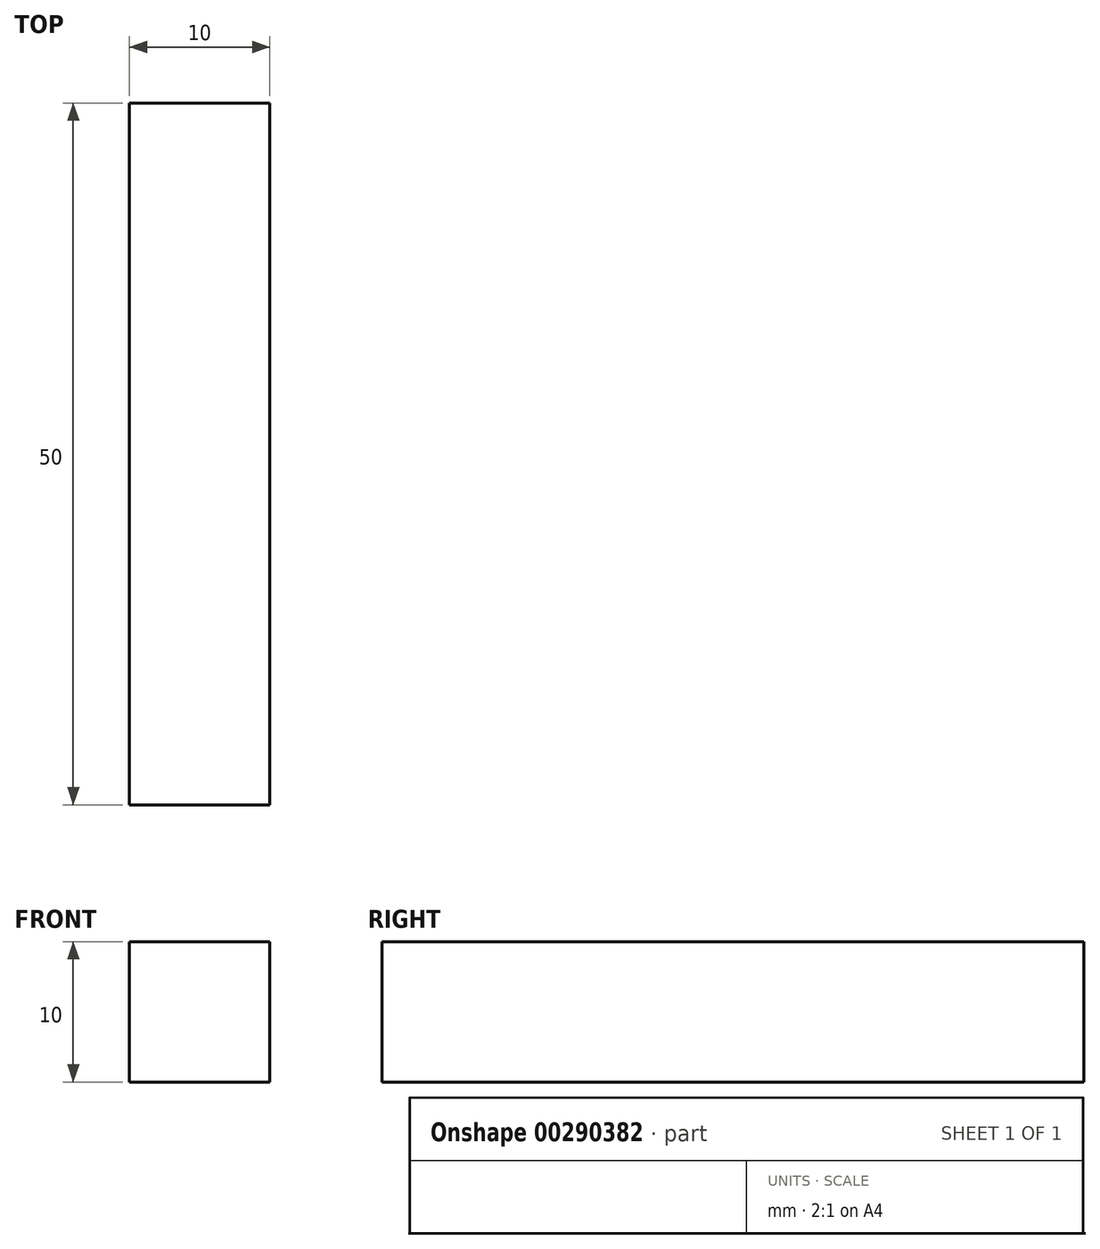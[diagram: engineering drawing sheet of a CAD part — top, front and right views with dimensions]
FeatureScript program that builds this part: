
annotation { "Feature Type Name" : "Feature", "Feature Type Description" : "" }
export const myFeature = defineFeature(function(context is Context, id is Id, definition is map)
    precondition{}
    {
        {
            var Q0;
            Q0=qCreatedBy(makeId("Front.planeOp"),FACE);
            var sketch = newSketch(context, id + "F0", { "sketchPlane" : qUnion([Q0])});
            skLineSegment(sketch, "E0.bottom", {"start": v(5, 5) * mm, "end": v(-5, 5) * mm});
            skLineSegment(sketch, "E0.top", {"start": v(5, -5) * mm, "end": v(-5, -5) * mm});
            skLineSegment(sketch, "E0.left", {"start": v(5, 5) * mm, "end": v(5, -5) * mm});
            skLineSegment(sketch, "E0.right", {"start": v(-5, 5) * mm, "end": v(-5, -5) * mm});
            skPoint(sketch, "E0.middle", {"position": v(0, 0) * mm});
            skSolve(sketch);
        }
        {
            var Q0;
            Q0 = qSketchRegion(id + "F0", true);
            extrude(context, id + "F1", {"entities" : qUnion([Q0]), "endBound" : BoundingType.SYMMETRIC, "depth" : 50 * mm});
        }
    });
